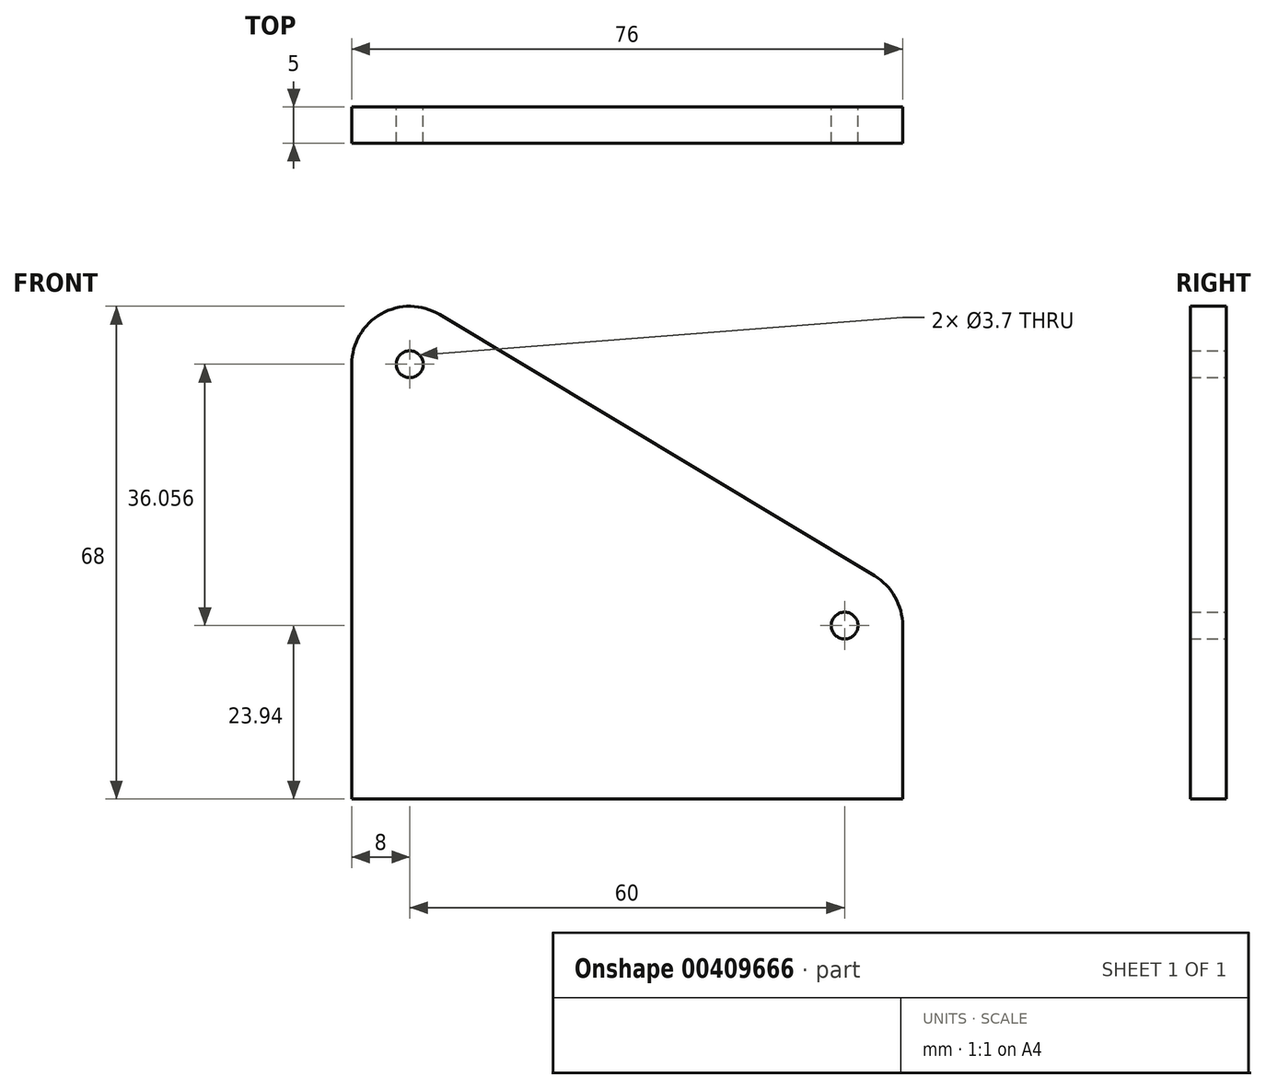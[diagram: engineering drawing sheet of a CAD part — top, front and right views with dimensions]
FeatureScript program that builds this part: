
annotation { "Feature Type Name" : "Feature", "Feature Type Description" : "" }
export const myFeature = defineFeature(function(context is Context, id is Id, definition is map)
    precondition{}
    {
        {
            var Q0;
            Q0=qCreatedBy(makeId("Front.planeOp"),FACE);
            var sketch = newSketch(context, id + "F0", { "sketchPlane" : qUnion([Q0])});
            skCircle(sketch, "E0", {"center": v(-60, 36.06) * mm, "radius": 1.85 * mm});
            skCircle(sketch, "E1", {"center": v(0, 0) * mm, "radius": 1.85 * mm});
            skArc(sketch, "E2", {"start": v(-55.88, 42.91) * mm, "mid": v(-63.94, 43.02) * mm, "end": v(-68, 36.06) * mm});
            skArc(sketch, "E3", {"start": v(8, 0) * mm, "mid": v(6.96, 3.94) * mm, "end": v(4.12, 6.86) * mm});
            skLineSegment(sketch, "E4", {"start": v(4.12, 6.86) * mm, "end": v(-55.88, 42.91) * mm});
            skLineSegment(sketch, "E5", {"start": v(8, 0) * mm, "end": v(8, -23.94) * mm});
            skLineSegment(sketch, "E6", {"start": v(8, -23.94) * mm, "end": v(-68, -23.94) * mm});
            skLineSegment(sketch, "E7", {"start": v(-68, 36.06) * mm, "end": v(-68, -23.94) * mm});
            skSolve(sketch);
        }
        {
            var Q0;
            {var subQ3=sQuery(id+"F0.wireOp",EDGE,"sDuS7eFg-11l1-5X3t-srPq-atH7HsszrKK6");Q0=makeQuery(id+"F0.imprint","IMPRINT",FACE,{"disambiguationData":[TD([[makeQuery(id+"F0.imprint","IMPRINT",EDGE,{"derivedFrom":subQ3}),-1.0]])]});}
            var Q1;
            Q1=makeQuery(id+"F0.imprint","IMPRINT",FACE,{"disambiguationData":[TD([[makeQuery(id+"F0.imprint","IMPRINT",EDGE,{"derivedFrom":sQuery(id+"F0.wireOp",EDGE,"E0")}),-1.0]])]});
            var Q2;
            Q2=makeQuery(id+"F0.imprint","IMPRINT",FACE,{"disambiguationData":[TD([[makeQuery(id+"F0.imprint","IMPRINT",EDGE,{"derivedFrom":sQuery(id+"F0.wireOp",EDGE,"E1")}),-1.0]])]});
            var Q3;
            Q3=makeQuery(id+"F0.imprint","IMPRINT",FACE,{"disambiguationData":[TD([[makeQuery(id+"F0.imprint","IMPRINT",EDGE,{"derivedFrom":sQuery(id+"F0.wireOp",EDGE,"z6FmBHHr-gBKJ-RHjl-6y1z-E9lHECQuajrI")}),-1.0]])]});
            extrude(context, id + "F1", {"entities" : qUnion([Q0, Q1, Q2, Q3]), "endBound" : BoundingType.SYMMETRIC, "depth" : 5 * mm});
        }
    });
